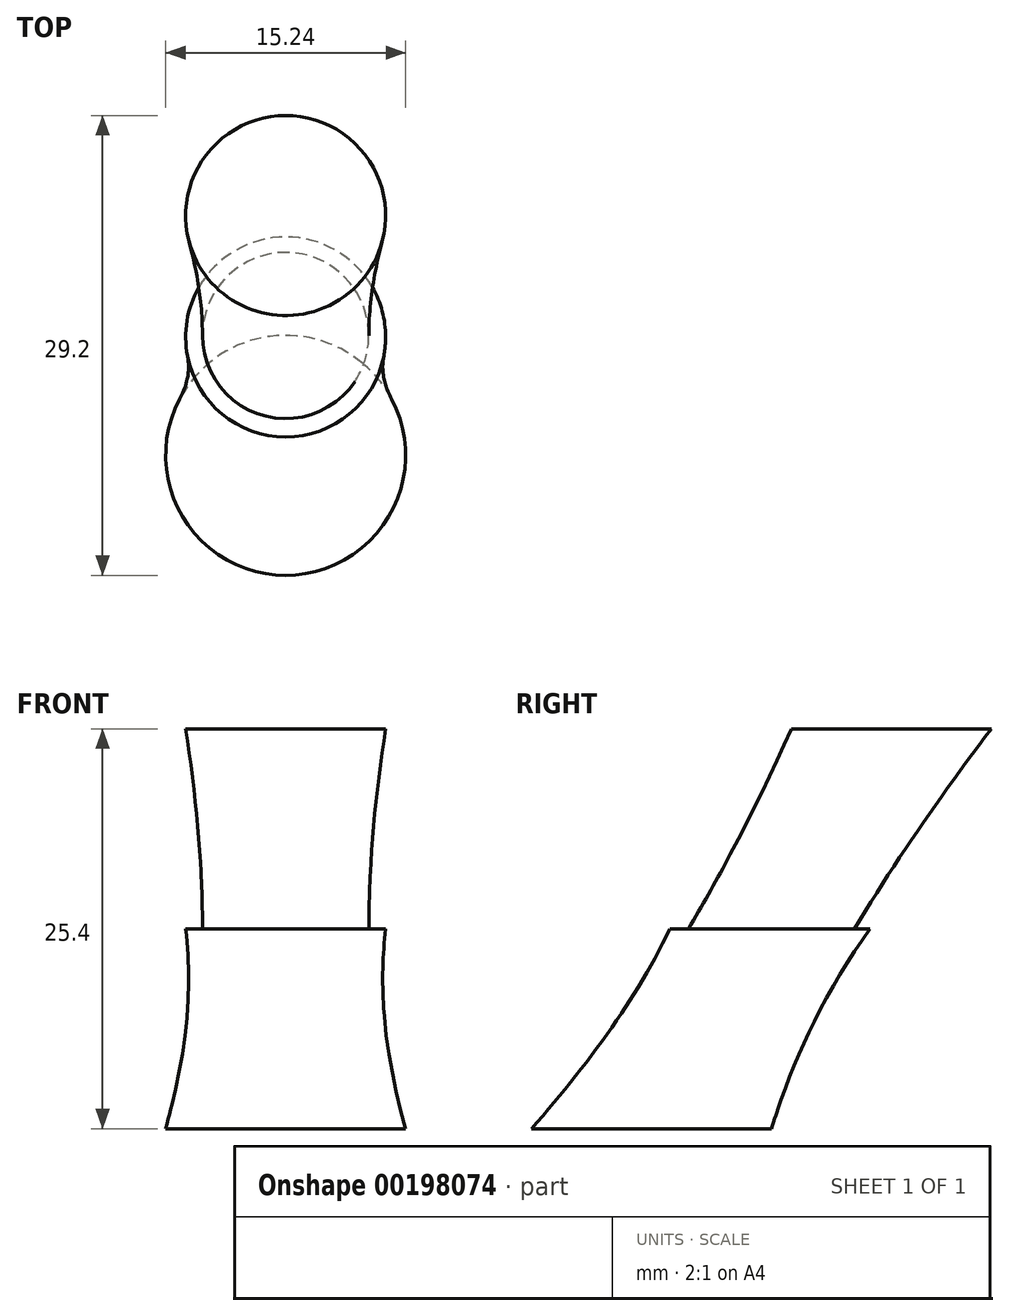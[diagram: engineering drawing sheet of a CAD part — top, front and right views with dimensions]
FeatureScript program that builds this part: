
annotation { "Feature Type Name" : "Feature", "Feature Type Description" : "" }
export const myFeature = defineFeature(function(context is Context, id is Id, definition is map)
    precondition{}
    {
        {
            var Q0;
            Q0=qCreatedBy(makeId("Top.planeOp"),FACE);
            var sketch = newSketch(context, id + "F0", { "sketchPlane" : qUnion([Q0])});
            skCircle(sketch, "E0", {"center": v(0, 0) * mm, "radius": 6.35 * mm});
            skSolve(sketch);
        }
        {
            var Q0;
            Q0=qCreatedBy(makeId("Top.planeOp"),FACE);
            cPlane(context, id + "F1", {"entities" : qUnion([Q0]), "cplaneType" : CPlaneType.OFFSET, "offset" : 25.4 * mm, "width" : 152.4 * mm, "height" : 152.4 * mm});
        }
        {
            var Q0;
            Q0=qCreatedBy(makeId("Right.planeOp"),FACE);
            var sketch = newSketch(context, id + "F2", { "sketchPlane" : qUnion([Q0])});
            skLineSegment(sketch, "E1", {"start": v(0, 0) * mm, "end": v(30.46, 52.75) * mm, "construction": true});
            skLineSegment(sketch, "E2", {"start": v(0, 0) * mm, "end": v(31.22, 0) * mm, "construction": true});
            skSolve(sketch);
        }
        {
            var Q0;
            Q0=qCreatedBy(id+"F1.planeOp",FACE);
            var sketch = newSketch(context, id + "F3", { "sketchPlane" : qUnion([Q0])});
            skLineSegment(sketch, "E3.0", {"start": v(0, 0) * mm, "end": v(0, 30.46) * mm, "construction": true});
            skCircle(sketch, "E4", {"center": v(0, 15.23) * mm, "radius": 6.35 * mm});
            skSolve(sketch);
        }
        {
            var Q0;
            Q0=makeQuery(id+"F0.imprint","IMPRINT",FACE,{"disambiguationData":[TD([[makeQuery(id+"F0.imprint","IMPRINT",EDGE,{"derivedFrom":sQuery(id+"F0.wireOp",EDGE,"E0")}),1.0]])]});
            var Q1;
            Q1=makeQuery(id+"F3.imprint","IMPRINT",FACE,{"disambiguationData":[TD([[makeQuery(id+"F3.imprint","IMPRINT",EDGE,{"derivedFrom":sQuery(id+"F3.wireOp",EDGE,"E4")}),1.0]])]});
            loft(context, id + "F4", {"sheetProfilesArray" : [{ "sheetProfileEntities" : qUnion([Q0]) }, { "sheetProfileEntities" : qUnion([Q1]) }]});
        }
        {
            var Q0;
            Q0=qCreatedBy(makeId("Top.planeOp"),FACE);
            var sketch = newSketch(context, id + "F5", { "sketchPlane" : qUnion([Q0])});
            skCircle(sketch, "E5", {"center": v(0, 0) * mm, "radius": 7.62 * mm});
            skSolve(sketch);
        }
        {
            var Q0;
            Q0=qCreatedBy(id+"F1.planeOp",FACE);
            cPlane(context, id + "F6", {"entities" : qUnion([Q0]), "cplaneType" : CPlaneType.OFFSET, "offset" : 12.7 * mm, "oppositeDirection" : true, "width" : 152.4 * mm, "height" : 152.4 * mm});
        }
        {
            var Q0;
            Q0=qCreatedBy(id+"F6.planeOp",FACE);
            var sketch = newSketch(context, id + "F7", { "sketchPlane" : qUnion([Q0])});
            skLineSegment(sketch, "E6.0", {"start": v(0, 0) * mm, "end": v(0, 30.46) * mm, "construction": true});
            skCircle(sketch, "E7", {"center": v(0, 7.52) * mm, "radius": 6.35 * mm});
            skSolve(sketch);
        }
        {
            var Q1;
            Q1=makeQuery(id+"F7.imprint","IMPRINT",FACE,{"disambiguationData":[TD([[makeQuery(id+"F7.imprint","IMPRINT",EDGE,{"derivedFrom":sQuery(id+"F7.wireOp",EDGE,"E7")}),1.0]])]});
            var Q2;
            Q2=makeQuery(id+"F5.imprint","IMPRINT",FACE,{"disambiguationData":[TD([[makeQuery(id+"F5.imprint","IMPRINT",EDGE,{"derivedFrom":sQuery(id+"F5.wireOp",EDGE,"E5")}),1.0]])]});
            loft(context, id + "F8", {"operationType" : NewBodyOperationType.ADD, "sheetProfilesArray" : [{ "sheetProfileEntities" : qUnion([Q1]) }, { "sheetProfileEntities" : qUnion([Q2]) }]});
        }
    });
